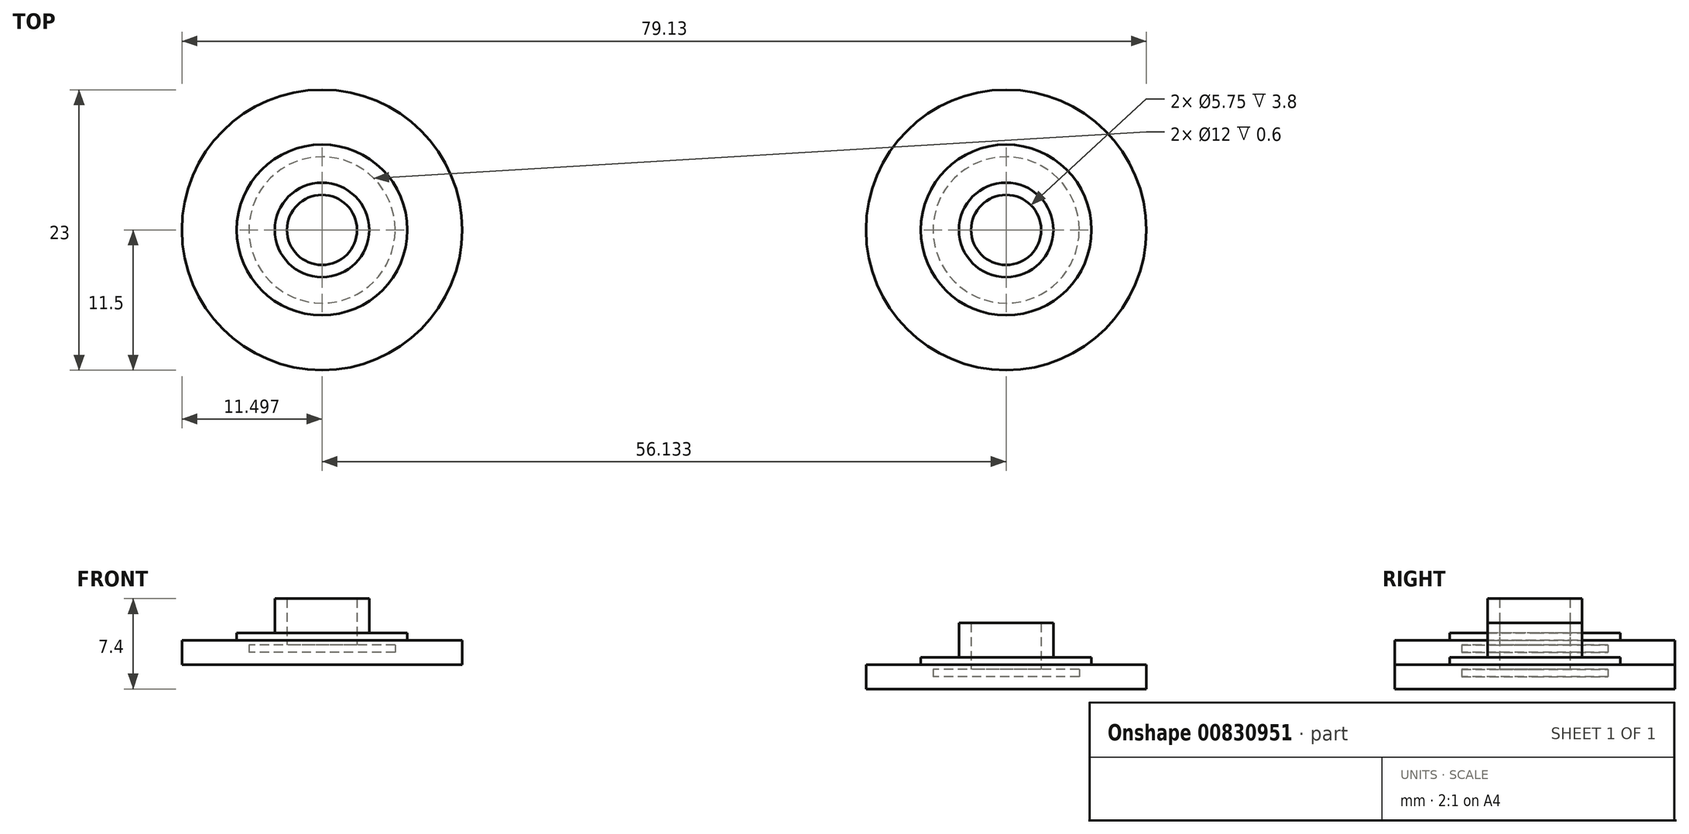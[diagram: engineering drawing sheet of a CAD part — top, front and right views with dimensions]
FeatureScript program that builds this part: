
annotation { "Feature Type Name" : "Feature", "Feature Type Description" : "" }
export const myFeature = defineFeature(function(context is Context, id is Id, definition is map)
    precondition{}
    {
        {
            var Q0;
            Q0=qCreatedBy(makeId("Top.planeOp"),FACE);
            var sketch = newSketch(context, id + "F0", { "sketchPlane" : qUnion([Q0])});
            skCircle(sketch, "E0", {"center": v(0, 0) * mm, "radius": 3.88 * mm});
            skCircle(sketch, "E1", {"center": v(0, 0) * mm, "radius": 7 * mm});
            skCircle(sketch, "E2", {"center": v(0, 0) * mm, "radius": 11.5 * mm});
            skSolve(sketch);
        }
        {
            var Q0;
            Q0=makeQuery(id+"F0.imprint","IMPRINT",FACE,{"disambiguationData":[TD([[makeQuery(id+"F0.imprint","IMPRINT",EDGE,{"derivedFrom":sQuery(id+"F0.wireOp",EDGE,"E0")}),1.0]])]});
            extrude(context, id + "F1", {"entities" : qUnion([Q0]), "depth" : 3.4 * mm, "offsetDistance" : 25 * mm});
        }
        {
            var Q0;
            Q0=makeQuery(id+"F0.imprint","IMPRINT",FACE,{"disambiguationData":[TD([[makeQuery(id+"F0.imprint","IMPRINT",EDGE,{"derivedFrom":sQuery(id+"F0.wireOp",EDGE,"E0")}),-1.0]])]});
            extrude(context, id + "F2", {"entities" : qUnion([Q0]), "operationType" : NewBodyOperationType.ADD, "depth" : 0.6 * mm, "offsetDistance" : 25 * mm});
        }
        {
            var Q0;
            Q0=makeQuery(id+"F0.imprint","IMPRINT",FACE,{"disambiguationData":[TD([[makeQuery(id+"F0.imprint","IMPRINT",EDGE,{"derivedFrom":sQuery(id+"F0.wireOp",EDGE,"E0")}),-1.0]])]});
            var Q1;
            Q1=makeQuery(id+"F0.imprint","IMPRINT",FACE,{"disambiguationData":[TD([[makeQuery(id+"F0.imprint","IMPRINT",EDGE,{"derivedFrom":sQuery(id+"F0.wireOp",EDGE,"E0")}),1.0]])]});
            var Q2;
            Q2=makeQuery(id+"F0.imprint","IMPRINT",FACE,{"disambiguationData":[TD([[makeQuery(id+"F0.imprint","IMPRINT",EDGE,{"derivedFrom":sQuery(id+"F0.wireOp",EDGE,"E1")}),-1.0]])]});
            extrude(context, id + "F3", {"entities" : qUnion([Q0, Q1, Q2]), "operationType" : NewBodyOperationType.ADD, "oppositeDirection" : true, "depth" : 2 * mm, "offsetDistance" : 25 * mm});
        }
        {
            var Q0;
            Q0=makeQuery(id+"F1.opExtrude","CAP_FACE",FACE,{"disambiguationData":[OSD([sQuery(id+"F0.wireOp",EDGE,"E0")])],"isStart":false});
            shell(context, id + "F4", {"entities" : qUnion([Q0]), "thickness" : 1 * mm});
        }
        {
            var Q0;
            Q0=qCreatedBy(makeId("Top.planeOp"),FACE);
            var sketch = newSketch(context, id + "F5", { "sketchPlane" : qUnion([Q0])});
            skCircle(sketch, "E3", {"center": v(-56.13, 0) * mm, "radius": 3.88 * mm});
            skCircle(sketch, "E4", {"center": v(-56.13, 0) * mm, "radius": 7 * mm});
            skCircle(sketch, "E5", {"center": v(-56.13, 0) * mm, "radius": 11.5 * mm});
            skSolve(sketch);
        }
        {
            var Q0;
            Q0=makeQuery(id+"F5.imprint","IMPRINT",FACE,{"disambiguationData":[TD([[makeQuery(id+"F5.imprint","IMPRINT",EDGE,{"derivedFrom":sQuery(id+"F5.wireOp",EDGE,"E3")}),1.0]])]});
            extrude(context, id + "F6", {"entities" : qUnion([Q0]), "depth" : 3.4 * mm, "offsetDistance" : 25 * mm});
        }
        {
            var Q0;
            Q0=makeQuery(id+"F5.imprint","IMPRINT",FACE,{"disambiguationData":[TD([[makeQuery(id+"F5.imprint","IMPRINT",EDGE,{"derivedFrom":sQuery(id+"F5.wireOp",EDGE,"E3")}),-1.0]])]});
            extrude(context, id + "F7", {"entities" : qUnion([Q0]), "operationType" : NewBodyOperationType.ADD, "depth" : 0.6 * mm, "offsetDistance" : 25 * mm});
        }
        {
            var Q0;
            Q0=makeQuery(id+"F6.opExtrude","CAP_FACE",FACE,{"disambiguationData":[OSD([sQuery(id+"F5.wireOp",EDGE,"E3")])],"isStart":false});
            var Q1;
            Q1=makeQuery(id+"F7.opExtrude","CAP_FACE",FACE,{"disambiguationData":[OSD([sQuery(id+"F5.wireOp",EDGE,"E3"),sQuery(id+"F5.wireOp",EDGE,"E4")])],"isStart":false});
            var Q2;
            Q2=makeQuery(id+"F5.imprint","IMPRINT",FACE,{"disambiguationData":[TD([[makeQuery(id+"F5.imprint","IMPRINT",EDGE,{"derivedFrom":sQuery(id+"F5.wireOp",EDGE,"E4")}),-1.0]])]});
            var Q3;
            Q3=makeQuery(id+"F5.imprint","IMPRINT",FACE,{"disambiguationData":[TD([[makeQuery(id+"F5.imprint","IMPRINT",EDGE,{"derivedFrom":sQuery(id+"F5.wireOp",EDGE,"E3")}),1.0]])]});
            extrude(context, id + "F8", {"entities" : qUnion([Q0, Q1, Q2, Q3]), "operationType" : NewBodyOperationType.ADD, "depth" : 2 * mm, "offsetDistance" : 25 * mm});
        }
        {
            var Q0;
            {var subQ0=sQuery(id+"F5.wireOp",EDGE,"E3");Q0=makeQuery(id+"F8.opExtrude","CAP_FACE",FACE,{"disambiguationData":[OSD([subQ0]),TDD([makeQuery(id+"F6.opExtrude","CAP_FACE",FACE,{"disambiguationData":[OSD([subQ0])],"isStart":false})])],"isStart":false});}
            shell(context, id + "F9", {"entities" : qUnion([Q0]), "thickness" : 1 * mm});
        }
    });
